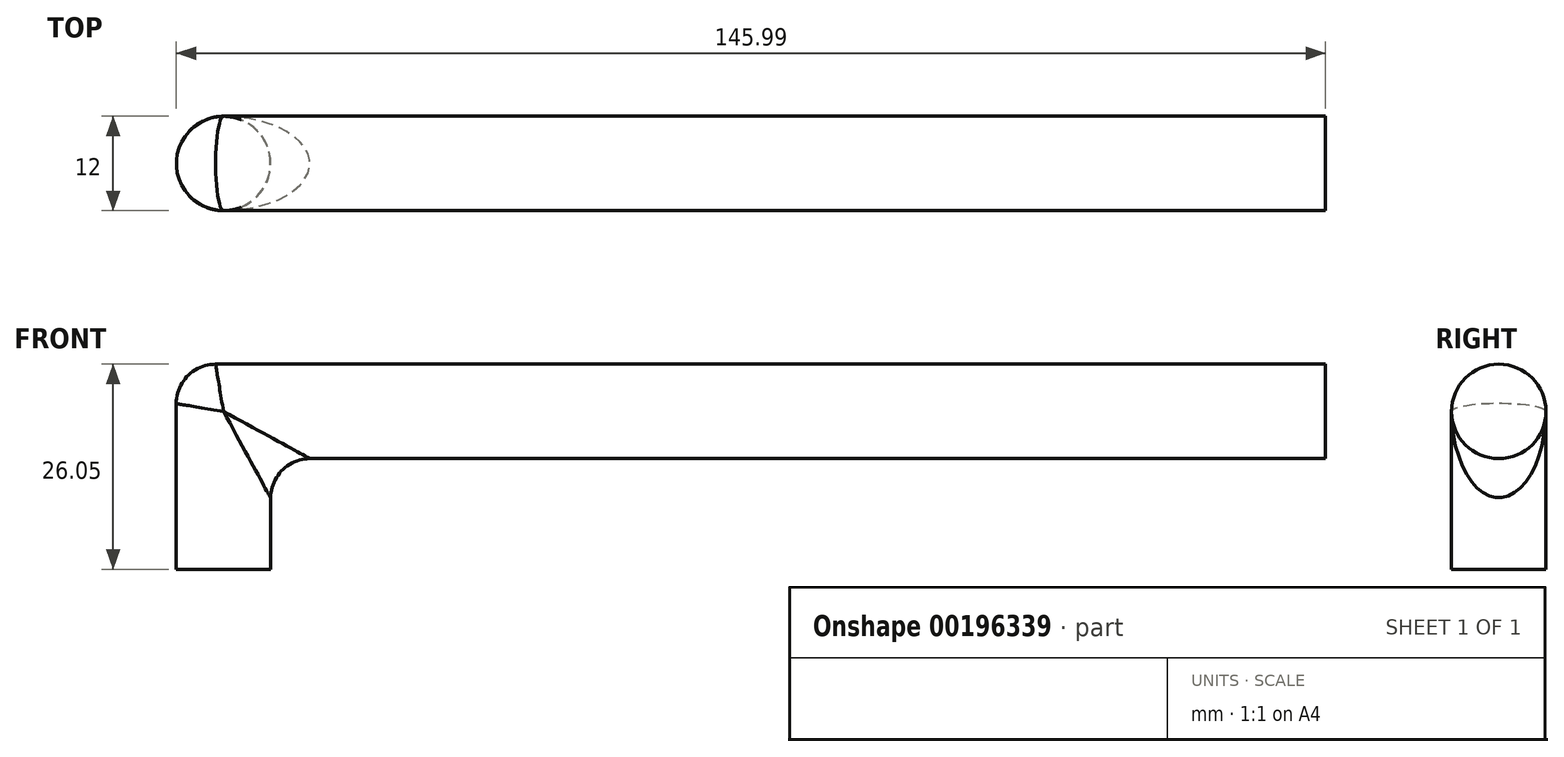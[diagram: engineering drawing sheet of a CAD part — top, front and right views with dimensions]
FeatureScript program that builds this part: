
annotation { "Feature Type Name" : "Feature", "Feature Type Description" : "" }
export const myFeature = defineFeature(function(context is Context, id is Id, definition is map)
    precondition{}
    {
        {
            var Q0;
            Q0=qCreatedBy(makeId("Right.planeOp"),FACE);
            var sketch = newSketch(context, id + "F0", { "sketchPlane" : qUnion([Q0])});
            skCircle(sketch, "E0", {"center": v(0, 0) * mm, "radius": 6 * mm});
            skSolve(sketch);
        }
        {
            var Q0;
            Q0=makeQuery(id+"F0.imprint","IMPRINT",FACE,{"disambiguationData":[TD([[makeQuery(id+"F0.imprint","IMPRINT",EDGE,{"derivedFrom":sQuery(id+"F0.wireOp",EDGE,"E0")}),1.0]])]});
            extrude(context, id + "F1", {"entities" : qUnion([Q0]), "depth" : 130 * mm});
        }
        {
            var Q0;
            Q0=qCreatedBy(makeId("Front.planeOp"),FACE);
            var sketch = newSketch(context, id + "F2", { "sketchPlane" : qUnion([Q0])});
            skLineSegment(sketch, "E1", {"start": v(0, 0) * mm, "end": v(-10, 0) * mm});
            skLineSegment(sketch, "E2", {"start": v(-10, 0) * mm, "end": v(-10, -20.05) * mm});
            skSolve(sketch);
        }
        {
            var Q0;
            Q0=makeQuery(id+"F1.opExtrude","CAP_FACE",FACE,{"disambiguationData":[OSD([sQuery(id+"F0.wireOp",EDGE,"E0")])],"isStart":true});
            var Q1;
            Q1=sQuery(id+"F2.wireOp",EDGE,"E2");
            var Q2;
            Q2=sQuery(id+"F2.wireOp",EDGE,"E1");
            sweep(context, id + "F3", {"operationType" : NewBodyOperationType.ADD, "profiles" : qUnion([Q0]), "path" : qUnion([Q1, Q2])});
        }
        {
            var Q0;
            Q0=makeQuery(id+"F3.opSweep","MID_CAP_EDGE",EDGE,{"disambiguationData":[OSD([sQuery(id+"F0.wireOp",EDGE,"E0"),sQuery(id+"F2.wireOp",VERTEX,"E1.end")])],"capPos":1.0});
            fillet(context, id + "F4", {"entities" : qUnion([Q0]), "radius" : 5 * mm, "tangentPropagation" : true, "allowEdgeOverflow" : false});
        }
    });
